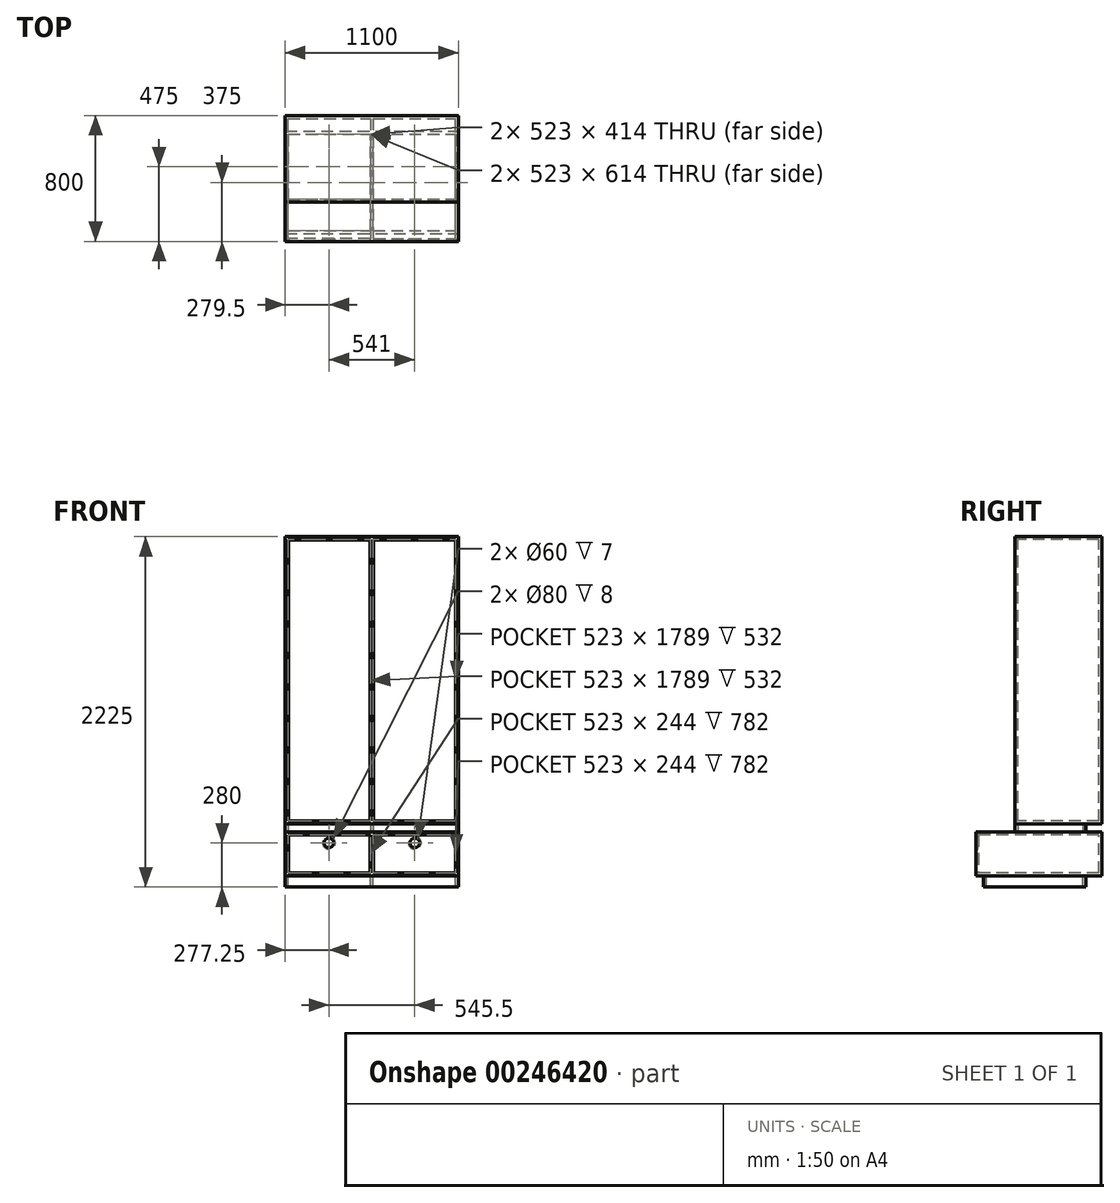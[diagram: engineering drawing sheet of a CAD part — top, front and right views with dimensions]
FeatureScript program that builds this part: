
annotation { "Feature Type Name" : "Feature", "Feature Type Description" : "" }
export const myFeature = defineFeature(function(context is Context, id is Id, definition is map)
    precondition{}
    {
        {
            var Q0;
            Q0=qCreatedBy(makeId("Top.planeOp"),FACE);
            var sketch = newSketch(context, id + "F0", { "sketchPlane" : qUnion([Q0])});
            skLineSegment(sketch, "E0.bottom", {"start": v(0, 0) * mm, "end": v(-1100, 0) * mm});
            skLineSegment(sketch, "E0.top", {"start": v(0, 800) * mm, "end": v(-1100, 800) * mm});
            skLineSegment(sketch, "E0.left", {"start": v(0, 0) * mm, "end": v(0, 800) * mm});
            skLineSegment(sketch, "E0.right", {"start": v(-1100, 0) * mm, "end": v(-1100, 800) * mm});
            skSolve(sketch);
        }
        {
            var Q0;
            Q0=makeQuery(id+"F0.imprint","IMPRINT",FACE,{"disambiguationData":[TD([[makeQuery(id+"F0.imprint","IMPRINT",EDGE,{"derivedFrom":sQuery(id+"F0.wireOp",EDGE,"E0.bottom")}),-1.0]])]});
            extrude(context, id + "F1", {"entities" : qUnion([Q0]), "depth" : (350 - 70) * mm});
        }
        {
            var Q0;
            Q0=makeQuery(id+"F1.opExtrude","SWEPT_FACE",FACE,{"disambiguationData":[OSD([sQuery(id+"F0.wireOp",EDGE,"E0.bottom")])]});
            shell(context, id + "F2", {"entities" : qUnion([Q0]), "thickness" : 18 * mm});
        }
        {
            var Q0;
            Q0=makeQuery(id+"F1.opExtrude","SWEPT_FACE",FACE,{"disambiguationData":[OSD([sQuery(id+"F0.wireOp",EDGE,"E0.bottom")])]});
            var sketch = newSketch(context, id + "F3", { "sketchPlane" : qUnion([Q0])});
            skLineSegment(sketch, "E1.bottom", {"start": v(-559, 262) * mm, "end": v(-541, 262) * mm});
            skLineSegment(sketch, "E1.top", {"start": v(-559, 18) * mm, "end": v(-541, 18) * mm});
            skLineSegment(sketch, "E1.left", {"start": v(-559, 262) * mm, "end": v(-559, 18) * mm});
            skLineSegment(sketch, "E1.right", {"start": v(-541, 262) * mm, "end": v(-541, 18) * mm});
            skSolve(sketch);
        }
        {
            var Q0;
            Q0=qSketchRegion(id+"F3",true);
            var Q1;
            Q1=makeQuery(id+"F2.opShell","OFFSET_FACE",FACE,{"disambiguationData":[OSD([sQuery(id+"F0.wireOp",EDGE,"E0.top")])]});
            extrude(context, id + "F4", {"entities" : qUnion([Q0]), "operationType" : NewBodyOperationType.ADD, "endBound" : BoundingType.UP_TO_SURFACE, "oppositeDirection" : true, "endBoundEntityFace" : qUnion([Q1]), "depth" : 25 * mm});
        }
        {
            var Q0;
            Q0=makeQuery(id+"F4.boolean.opBoolean","MERGE",FACE,{"derivedFrom":[makeQuery(id+"F1.opExtrude","SWEPT_FACE",FACE,{"disambiguationData":[OSD([sQuery(id+"F0.wireOp",EDGE,"E0.bottom")])]}),makeQuery(id+"F4.opExtrude","CAP_FACE",FACE,{"disambiguationData":[OSD([sQuery(id+"F3.wireOp",EDGE,"E1.bottom"),sQuery(id+"F3.wireOp",EDGE,"E1.top"),sQuery(id+"F3.wireOp",EDGE,"E1.left"),sQuery(id+"F3.wireOp",EDGE,"E1.right")])],"isStart":true})]});
            var sketch = newSketch(context, id + "F5", { "sketchPlane" : qUnion([Q0])});
            skLineSegment(sketch, "E2.0", {"start": v(-561, 260) * mm, "end": v(-1080, 260) * mm});
            skLineSegment(sketch, "E2.1", {"start": v(-561, 260) * mm, "end": v(-561, 20) * mm});
            skLineSegment(sketch, "E2.2", {"start": v(-561, 20) * mm, "end": v(-1080, 20) * mm});
            skLineSegment(sketch, "E2.3", {"start": v(-1080, 260) * mm, "end": v(-1080, 20) * mm});
            skSolve(sketch);
        }
        {
            var Q0;
            Q0=qSketchRegion(id+"F5",true);
            extrude(context, id + "F6", {"entities" : qUnion([Q0]), "oppositeDirection" : true, "depth" : 18 * mm});
        }
        {
            var Q0;
            Q0=makeQuery(id+"F1.opExtrude","SWEPT_FACE",FACE,{"disambiguationData":[OSD([sQuery(id+"F0.wireOp",EDGE,"E0.left")])]});
            cPlane(context, id + "F7", {"entities" : qUnion([Q0]), "cplaneType" : CPlaneType.OFFSET, "offset" : (1100 / 2) * mm, "oppositeDirection" : true, "width" : 150 * mm, "height" : 150 * mm});
        }
        {
            var Q0;
            Q0=makeQuery(id+"F6.opExtrude","CAP_FACE",FACE,{"disambiguationData":[OSD([sQuery(id+"F5.wireOp",EDGE,"E2.0"),sQuery(id+"F5.wireOp",EDGE,"E2.1"),sQuery(id+"F5.wireOp",EDGE,"E2.2"),sQuery(id+"F5.wireOp",EDGE,"E2.3")])],"isStart":true});
            var sketch = newSketch(context, id + "F8", { "sketchPlane" : qUnion([Q0])});
            skCircle(sketch, "E3", {"center": v(-822.75, 210) * mm, "radius": 30 * mm});
            skSolve(sketch);
        }
        {
            var Q0;
            Q0=qSketchRegion(id+"F8",true);
            extrude(context, id + "F9", {"entities" : qUnion([Q0]), "operationType" : NewBodyOperationType.REMOVE, "oppositeDirection" : true, "depth" : 15 * mm});
        }
        {
            var Q0;
            Q0=makeQuery(id+"F9.boolean.opBoolean","COPY",FACE,{"derivedFrom":makeQuery(id+"F9.opExtrude","CAP_FACE",FACE,{"disambiguationData":[OSD([sQuery(id+"F8.wireOp",EDGE,"E3")])],"isStart":false})});
            var sketch = newSketch(context, id + "F10", { "sketchPlane" : qUnion([Q0])});
            skCircle(sketch, "E4.0", {"center": v(-822.75, 210) * mm, "radius": 40 * mm});
            skSolve(sketch);
        }
        {
            var Q0;
            Q0=qSketchRegion(id+"F10",true);
            extrude(context, id + "F11", {"entities" : qUnion([Q0]), "operationType" : NewBodyOperationType.REMOVE, "depth" : 8 * mm});
        }
        {
            var Q0;
            Q0=makeQuery(id+"F6.opExtrude","SWEPT_BODY",BODY,{"disambiguationData":[OSD([sQuery(id+"F5.wireOp",EDGE,"E2.0"),sQuery(id+"F5.wireOp",EDGE,"E2.1"),sQuery(id+"F5.wireOp",EDGE,"E2.2"),sQuery(id+"F5.wireOp",EDGE,"E2.3")])]});
            var Q1;
            Q1=qCreatedBy(id+"F7.planeOp",FACE);
            mirror(context, id + "F12", {"entities" : qUnion([Q0]), "mirrorPlane" : qUnion([Q1])});
        }
        {
            var Q0;
            Q0=makeQuery(id+"F1.opExtrude","CAP_FACE",FACE,{"disambiguationData":[OSD([sQuery(id+"F0.wireOp",EDGE,"E0.bottom"),sQuery(id+"F0.wireOp",EDGE,"E0.top"),sQuery(id+"F0.wireOp",EDGE,"E0.left"),sQuery(id+"F0.wireOp",EDGE,"E0.right")])],"isStart":true});
            var sketch = newSketch(context, id + "F13", { "sketchPlane" : qUnion([Q0])});
            skLineSegment(sketch, "E5.bottom", {"start": v(-1100, -50) * mm, "end": v(0, -50) * mm});
            skLineSegment(sketch, "E5.top", {"start": v(-1100, -700) * mm, "end": v(0, -700) * mm});
            skLineSegment(sketch, "E5.left", {"start": v(-1100, -50) * mm, "end": v(-1100, -700) * mm});
            skLineSegment(sketch, "E5.right", {"start": v(0, -50) * mm, "end": v(0, -700) * mm});
            skLineSegment(sketch, "E6.0", {"start": v(-1082, -68) * mm, "end": v(-559, -68) * mm});
            skLineSegment(sketch, "E6.1", {"start": v(-1082, -68) * mm, "end": v(-1082, -682) * mm});
            skLineSegment(sketch, "E6.2", {"start": v(-1082, -682) * mm, "end": v(-559, -682) * mm});
            skLineSegment(sketch, "E6.3", {"start": v(-18, -68) * mm, "end": v(-18, -682) * mm});
            skLineSegment(sketch, "E7.left", {"start": v(-559, -68) * mm, "end": v(-559, -682) * mm});
            skLineSegment(sketch, "E7.right", {"start": v(-541, -68) * mm, "end": v(-541, -682) * mm});
            skLineSegment(sketch, "E8.trimOffspring", {"start": v(-541, -68) * mm, "end": v(-18, -68) * mm});
            skLineSegment(sketch, "E9.trimOffspring", {"start": v(-541, -682) * mm, "end": v(-18, -682) * mm});
            skSolve(sketch);
        }
        {
            var Q0;
            Q0 = qSketchRegion(id + "F13", true);
            extrude(context, id + "F14", {"entities" : qUnion([Q0]), "depth" : 70 * mm});
        }
        {
            var Q0;
            Q0=makeQuery(id+"F1.opExtrude","CAP_FACE",FACE,{"disambiguationData":[OSD([sQuery(id+"F0.wireOp",EDGE,"E0.bottom"),sQuery(id+"F0.wireOp",EDGE,"E0.top"),sQuery(id+"F0.wireOp",EDGE,"E0.left"),sQuery(id+"F0.wireOp",EDGE,"E0.right")])],"isStart":false});
            var sketch = newSketch(context, id + "F15", { "sketchPlane" : qUnion([Q0])});
            skLineSegment(sketch, "E10.bottom", {"start": v(-1100, 700) * mm, "end": v(0, 700) * mm});
            skLineSegment(sketch, "E10.top", {"start": v(-1100, 250) * mm, "end": v(0, 250) * mm});
            skLineSegment(sketch, "E10.left", {"start": v(-1100, 700) * mm, "end": v(-1100, 250) * mm});
            skLineSegment(sketch, "E10.right", {"start": v(0, 700) * mm, "end": v(0, 250) * mm});
            skLineSegment(sketch, "E11.0", {"start": v(-1082, 682) * mm, "end": v(-559, 682) * mm});
            skLineSegment(sketch, "E11.1", {"start": v(-1082, 682) * mm, "end": v(-1082, 268) * mm});
            skLineSegment(sketch, "E11.2", {"start": v(-1082, 268) * mm, "end": v(-559, 268) * mm});
            skLineSegment(sketch, "E11.3", {"start": v(-18, 682) * mm, "end": v(-18, 268) * mm});
            skLineSegment(sketch, "E12.left", {"start": v(-559, 682) * mm, "end": v(-559, 268) * mm});
            skLineSegment(sketch, "E12.right", {"start": v(-541, 682) * mm, "end": v(-541, 268) * mm});
            skLineSegment(sketch, "E13.trimOffspring", {"start": v(-541, 682) * mm, "end": v(-18, 682) * mm});
            skLineSegment(sketch, "E14.trimOffspring", {"start": v(-541, 268) * mm, "end": v(-18, 268) * mm});
            skSolve(sketch);
        }
        {
            var Q0;
            Q0 = qSketchRegion(id + "F15", true);
            extrude(context, id + "F16", {"entities" : qUnion([Q0]), "depth" : 50 * mm});
        }
        {
            var Q0;
            Q0=makeQuery(id+"F16.opExtrude","CAP_FACE",FACE,{"disambiguationData":[OSD([sQuery(id+"F15.wireOp",EDGE,"E10.bottom"),sQuery(id+"F15.wireOp",EDGE,"E10.top"),sQuery(id+"F15.wireOp",EDGE,"E10.left"),sQuery(id+"F15.wireOp",EDGE,"E10.right"),sQuery(id+"F15.wireOp",EDGE,"E11.0"),sQuery(id+"F15.wireOp",EDGE,"E11.1"),sQuery(id+"F15.wireOp",EDGE,"E11.2"),sQuery(id+"F15.wireOp",EDGE,"E11.3"),sQuery(id+"F15.wireOp",EDGE,"E12.left"),sQuery(id+"F15.wireOp",EDGE,"E12.right"),sQuery(id+"F15.wireOp",EDGE,"E13.trimOffspring"),sQuery(id+"F15.wireOp",EDGE,"E14.trimOffspring")])],"isStart":false});
            var sketch = newSketch(context, id + "F17", { "sketchPlane" : qUnion([Q0])});
            skLineSegment(sketch, "E15.bottom", {"start": v(-1100, 250) * mm, "end": v(0, 250) * mm});
            skLineSegment(sketch, "E15.top", {"start": v(-1100, 800) * mm, "end": v(0, 800) * mm});
            skLineSegment(sketch, "E15.left", {"start": v(-1100, 250) * mm, "end": v(-1100, 800) * mm});
            skLineSegment(sketch, "E15.right", {"start": v(0, 250) * mm, "end": v(0, 800) * mm});
            skSolve(sketch);
        }
        {
            var Q0;
            Q0 = qSketchRegion(id + "F17", true);
            extrude(context, id + "F18", {"entities" : qUnion([Q0]), "depth" : (2230 - 350 - 50 - 5) * mm});
        }
        {
            var Q0;
            Q0=makeQuery(id+"F18.opExtrude","SWEPT_FACE",FACE,{"disambiguationData":[OSD([sQuery(id+"F17.wireOp",EDGE,"E15.bottom")])]});
            shell(context, id + "F19", {"entities" : qUnion([Q0]), "thickness" : 18 * mm});
        }
        {
            var Q0;
            Q0=makeQuery(id+"F18.opExtrude","SWEPT_FACE",FACE,{"disambiguationData":[OSD([sQuery(id+"F17.wireOp",EDGE,"E15.bottom")])]});
            var sketch = newSketch(context, id + "F20", { "sketchPlane" : qUnion([Q0])});
            skLineSegment(sketch, "E16.bottom", {"start": v(-559, 348) * mm, "end": v(-541, 348) * mm});
            skLineSegment(sketch, "E16.top", {"start": v(-559, 2137) * mm, "end": v(-541, 2137) * mm});
            skLineSegment(sketch, "E16.left", {"start": v(-559, 348) * mm, "end": v(-559, 2137) * mm});
            skLineSegment(sketch, "E16.right", {"start": v(-541, 348) * mm, "end": v(-541, 2137) * mm});
            skSolve(sketch);
        }
        {
            var Q0;
            Q0 = qSketchRegion(id + "F20", true);
            extrude(context, id + "F21", {"entities" : qUnion([Q0]), "operationType" : NewBodyOperationType.ADD, "endBound" : BoundingType.UP_TO_NEXT, "oppositeDirection" : true, "depth" : 25 * mm});
        }
        {
            var Q0;
            Q0=makeQuery(id+"F21.boolean.opBoolean","MERGE",FACE,{"derivedFrom":[makeQuery(id+"F18.opExtrude","SWEPT_FACE",FACE,{"disambiguationData":[OSD([sQuery(id+"F17.wireOp",EDGE,"E15.bottom")])]}),makeQuery(id+"F21.opExtrude","CAP_FACE",FACE,{"disambiguationData":[OSD([sQuery(id+"F20.wireOp",EDGE,"E16.bottom"),sQuery(id+"F20.wireOp",EDGE,"E16.top"),sQuery(id+"F20.wireOp",EDGE,"E16.left"),sQuery(id+"F20.wireOp",EDGE,"E16.right"),sQuery(id+"F20.wireOp",EDGE,"gFGEFTyp-nEkA-kRGF-EtrJ-0ZU1zqqutEZT.bottom"),sQuery(id+"F20.wireOp",EDGE,"gFGEFTyp-nEkA-kRGF-EtrJ-0ZU1zqqutEZT.top"),sQuery(id+"F20.wireOp",EDGE,"gFGEFTyp-nEkA-kRGF-EtrJ-0ZU1zqqutEZT.left"),sQuery(id+"F20.wireOp",EDGE,"gFGEFTyp-nEkA-kRGF-EtrJ-0ZU1zqqutEZT.right")])],"isStart":true})]});
            var sketch = newSketch(context, id + "F22", { "sketchPlane" : qUnion([Q0])});
            skLineSegment(sketch, "E17.0", {"start": v(-1080, 350) * mm, "end": v(-561, 350) * mm});
            skLineSegment(sketch, "E17.1", {"start": v(-1080, 2135) * mm, "end": v(-1080, 350) * mm});
            skLineSegment(sketch, "E17.2", {"start": v(-561, 2135) * mm, "end": v(-1080, 2135) * mm});
            skLineSegment(sketch, "E17.3", {"start": v(-561, 350) * mm, "end": v(-561, 2135) * mm});
            skLineSegment(sketch, "E18.0", {"start": v(-20, 350) * mm, "end": v(-20, 2135) * mm});
            skLineSegment(sketch, "E18.1", {"start": v(-539, 350) * mm, "end": v(-20, 350) * mm});
            skLineSegment(sketch, "E18.2", {"start": v(-539, 2135) * mm, "end": v(-539, 350) * mm});
            skLineSegment(sketch, "E18.3", {"start": v(-20, 2135) * mm, "end": v(-539, 2135) * mm});
            skSolve(sketch);
        }
        {
            var Q0;
            Q0 = qSketchRegion(id + "F22", true);
            extrude(context, id + "F23", {"entities" : qUnion([Q0]), "oppositeDirection" : true, "depth" : 18 * mm});
        }
    });
